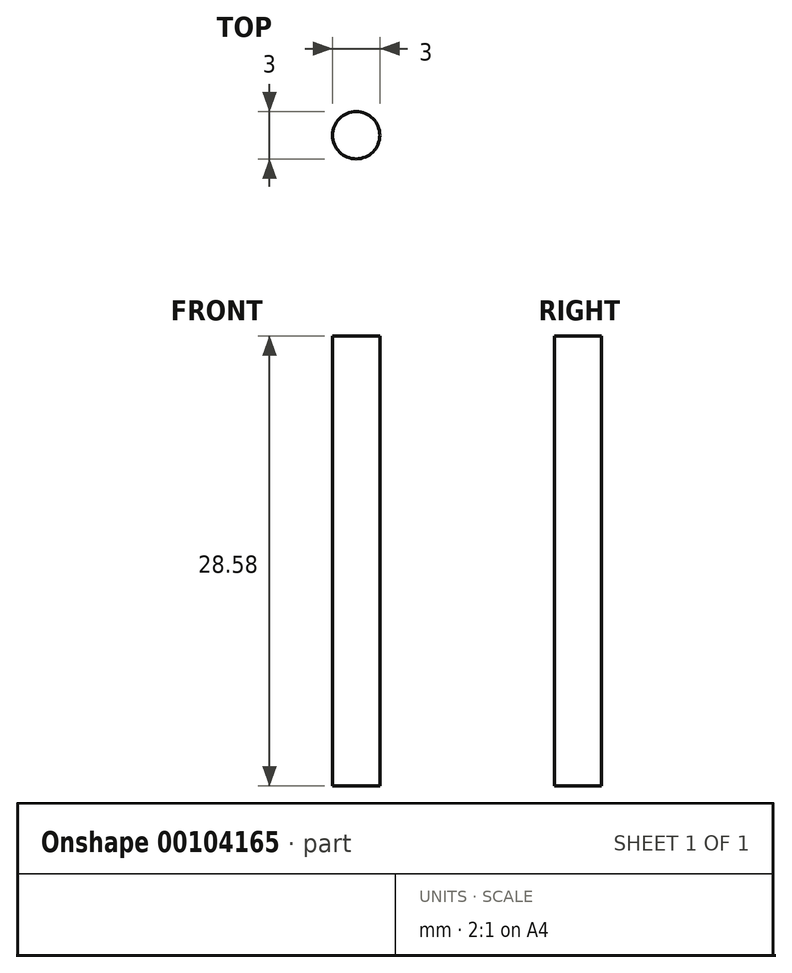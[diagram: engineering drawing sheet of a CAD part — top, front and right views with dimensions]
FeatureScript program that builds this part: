
annotation { "Feature Type Name" : "Feature", "Feature Type Description" : "" }
export const myFeature = defineFeature(function(context is Context, id is Id, definition is map)
    precondition{}
    {
        {
            var Q0;
            Q0=qCreatedBy(makeId("Top.planeOp"),FACE);
            var sketch = newSketch(context, id + "F0", { "sketchPlane" : qUnion([Q0])});
            skCircle(sketch, "E0", {"center": v(-52.28, -17.26) * mm, "radius": 1.5 * mm});
            skSolve(sketch);
        }
        {
            var Q0;
            Q0=makeQuery(id+"F0.imprint","IMPRINT",FACE,{"disambiguationData":[TD([[makeQuery(id+"F0.imprint","IMPRINT",EDGE,{"derivedFrom":sQuery(id+"F0.wireOp",EDGE,"E0")}),1.0]])]});
            extrude(context, id + "F1", {"entities" : qUnion([Q0]), "depth" : 28.57 * mm});
        }
    });
